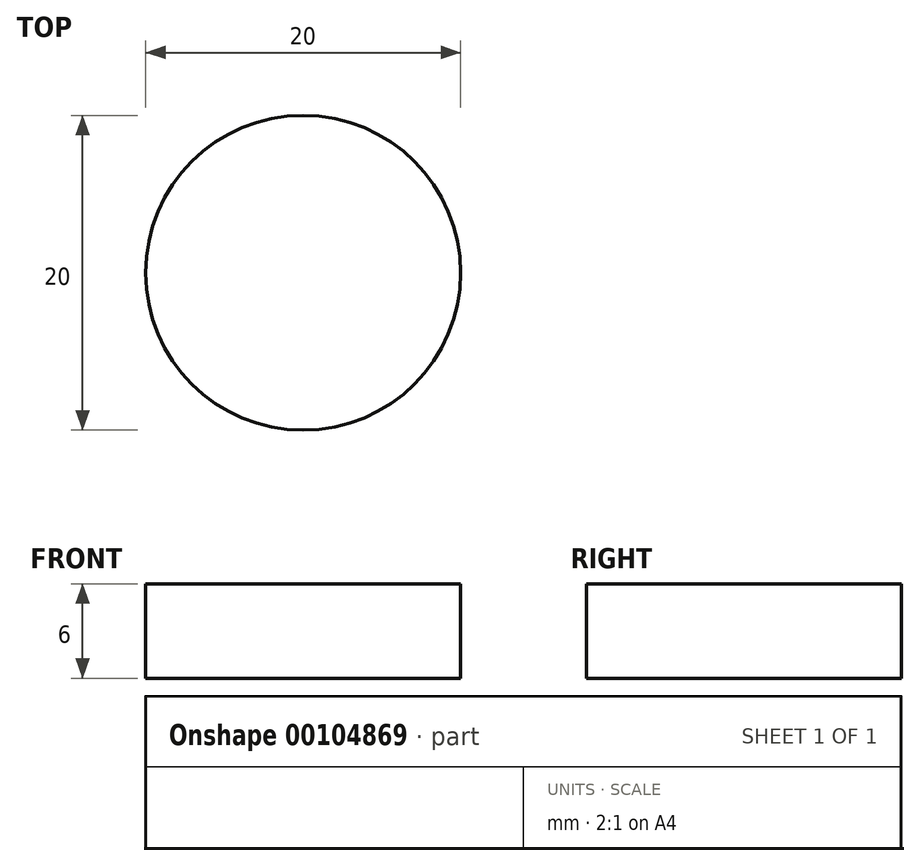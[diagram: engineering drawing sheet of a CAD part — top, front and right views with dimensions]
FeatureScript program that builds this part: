
annotation { "Feature Type Name" : "Feature", "Feature Type Description" : "" }
export const myFeature = defineFeature(function(context is Context, id is Id, definition is map)
    precondition{}
    {
        {
            var Q0;
            Q0=qCreatedBy(makeId("Top.planeOp"),FACE);
            var sketch = newSketch(context, id + "F0", { "sketchPlane" : qUnion([Q0])});
            skCircle(sketch, "E0", {"center": v(0, 0) * mm, "radius": 10 * mm});
            skSolve(sketch);
        }
        {
            var Q0;
            Q0=makeQuery(id+"F0.imprint","IMPRINT",FACE,{"disambiguationData":[TD([[makeQuery(id+"F0.imprint","IMPRINT",EDGE,{"derivedFrom":sQuery(id+"F0.wireOp",EDGE,"E0")}),1.0]])]});
            extrude(context, id + "F1", {"entities" : qUnion([Q0]), "depth" : 6 * mm});
        }
    });
